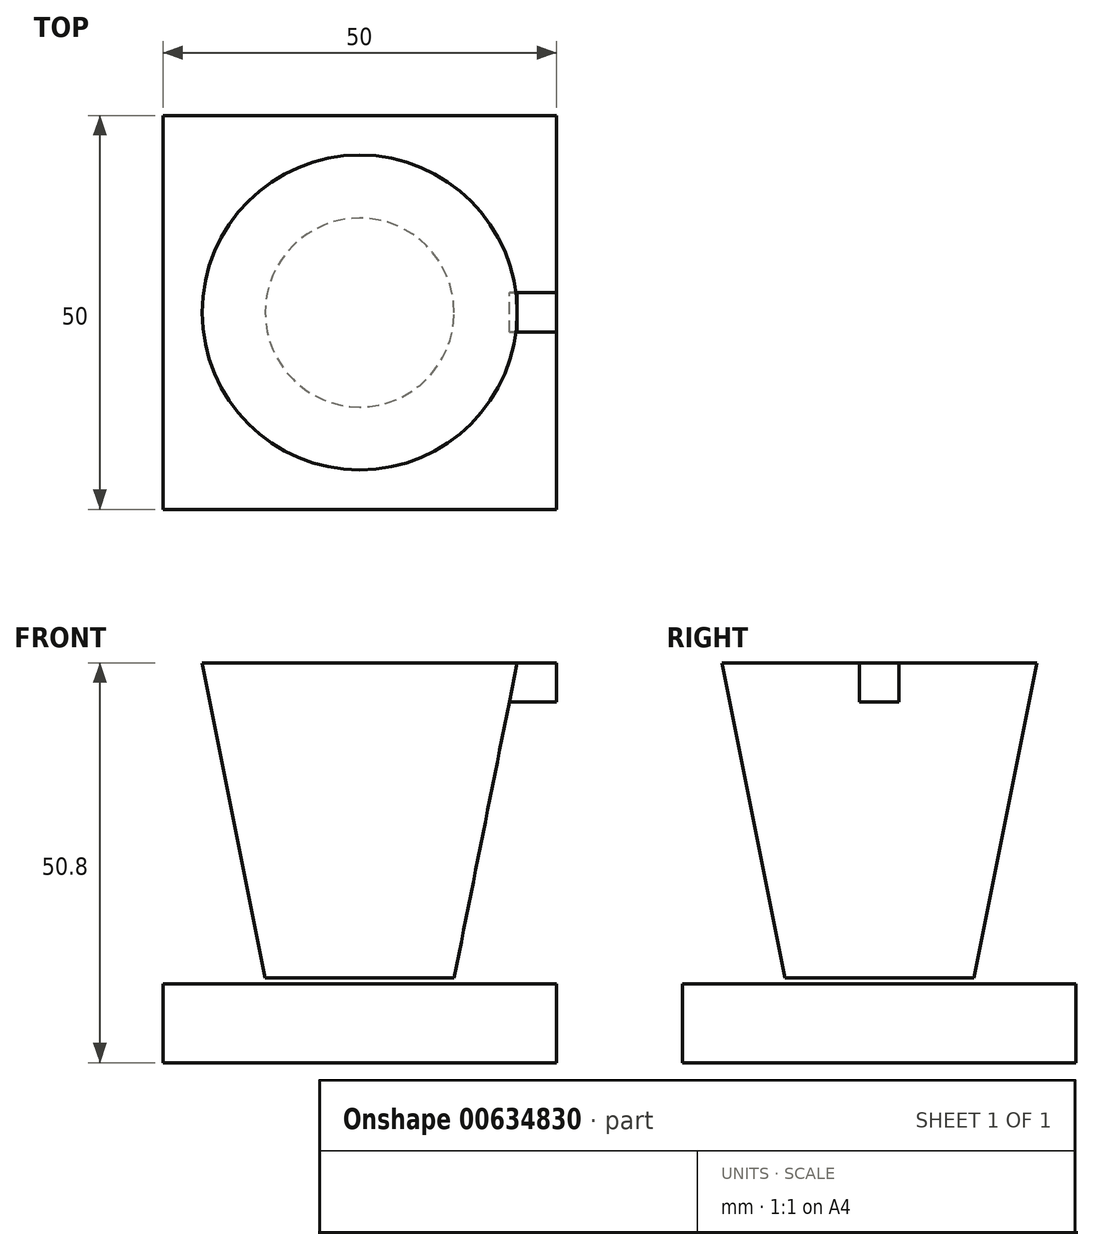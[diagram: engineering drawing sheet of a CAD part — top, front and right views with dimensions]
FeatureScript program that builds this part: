
annotation { "Feature Type Name" : "Feature", "Feature Type Description" : "" }
export const myFeature = defineFeature(function(context is Context, id is Id, definition is map)
    precondition{}
    {
        {
            var Q0;
            Q0=qCreatedBy(makeId("Front.planeOp"),FACE);
            var sketch = newSketch(context, id + "F0", { "sketchPlane" : qUnion([Q0])});
            skLineSegment(sketch, "E0.bottom", {"start": v(-25, 0) * mm, "end": v(25, 0) * mm});
            skLineSegment(sketch, "E0.top", {"start": v(-25, -10) * mm, "end": v(25, -10) * mm});
            skLineSegment(sketch, "E0.left", {"start": v(-25, 0) * mm, "end": v(-25, -10) * mm});
            skLineSegment(sketch, "E0.right", {"start": v(25, 0) * mm, "end": v(25, -10) * mm});
            skLineSegment(sketch, "E1", {"start": v(20, 40.8) * mm, "end": v(0, 40.8) * mm});
            skLineSegment(sketch, "E2", {"start": v(0, 40.8) * mm, "end": v(0, 0.8) * mm});
            skLineSegment(sketch, "E3.bottom", {"start": v(0, 40.8) * mm, "end": v(25, 40.8) * mm});
            skLineSegment(sketch, "E3.top", {"start": v(0, 35.8) * mm, "end": v(25, 35.8) * mm});
            skLineSegment(sketch, "E3.left", {"start": v(0, 40.8) * mm, "end": v(0, 35.8) * mm});
            skLineSegment(sketch, "E3.right", {"start": v(25, 40.8) * mm, "end": v(25, 35.8) * mm});
            skLineSegment(sketch, "E4.bottom", {"start": v(25, 35.8) * mm, "end": v(20, 35.8) * mm});
            skLineSegment(sketch, "E4.top", {"start": v(25, 0) * mm, "end": v(20, 0) * mm});
            skLineSegment(sketch, "E4.left", {"start": v(25, 35.8) * mm, "end": v(25, 0) * mm});
            skLineSegment(sketch, "E4.right", {"start": v(20, 35.8) * mm, "end": v(20, 0) * mm});
            skLineSegment(sketch, "E5", {"start": v(20, 40.8) * mm, "end": v(12, 0.8) * mm});
            skLineSegment(sketch, "E6", {"start": v(12, 0.8) * mm, "end": v(0, 0.8) * mm});
            skSolve(sketch);
        }
        {
            var Q0;
            Q0=makeQuery(id+"F0.imprint","IMPRINT",FACE,{"disambiguationData":[TD([[makeQuery(id+"F0.imprint","IMPRINT",EDGE,{"derivedFrom":sQuery(id+"F0.wireOp",EDGE,"E0.bottom")}),-1.0]])]});
            extrude(context, id + "F1", {"entities" : qUnion([Q0]), "endBound" : BoundingType.SYMMETRIC, "depth" : 50 * mm, "offsetDistance" : 25 * mm});
        }
        {
            var Q0;
            Q0=makeQuery(id+"F0.imprint","IMPRINT",FACE,{"disambiguationData":[TD([[makeQuery(id+"F0.imprint","IMPRINT",EDGE,{"derivedFrom":sQuery(id+"F0.wireOp",EDGE,"E4.bottom")}),1.0]])]});
            var Q1;
            {var subQ0=sQuery(id+"F0.wireOp",EDGE,"E3.right");Q1=makeQuery(id+"F0.imprint","IMPRINT",FACE,{"disambiguationData":[TD([[makeQuery(id+"F0.imprint","IMPRINT",EDGE,{"derivedFrom":subQ0}),-1.0]])]});}
            var Q2;
            {var subQ5=sQuery(id+"F0.wireOp",EDGE,"E3.left");Q2=makeQuery(id+"F0.imprint","IMPRINT",FACE,{"disambiguationData":[TD([[makeQuery(id+"F0.imprint","IMPRINT",EDGE,{"derivedFrom":subQ5}),1.0]])]});}
            extrude(context, id + "F2", {"entities" : qUnion([Q0, Q1, Q2]), "operationType" : NewBodyOperationType.ADD, "endBound" : BoundingType.SYMMETRIC, "depth" : 5 * mm, "offsetDistance" : 25 * mm});
        }
        {
            var Q0;
            {var subQ0=sQuery(id+"F0.wireOp",EDGE,"E2");Q0=makeQuery(id+"F0.imprint","IMPRINT",FACE,{"disambiguationData":[TD([[makeQuery(id+"F0.imprint","IMPRINT",EDGE,{"derivedFrom":subQ0}),1.0]])]});}
            var Q1;
            {var subQ5=sQuery(id+"F0.wireOp",EDGE,"E3.left");Q1=makeQuery(id+"F0.imprint","IMPRINT",FACE,{"disambiguationData":[TD([[makeQuery(id+"F0.imprint","IMPRINT",EDGE,{"derivedFrom":subQ5}),1.0]])]});}
            var Q2;
            Q2=sQuery(id+"F0.wireOp",EDGE,"E2");
            revolve(context, id + "F3", {"entities" : qUnion([Q0, Q1]), "axis" : qUnion([Q2]), "revolveType" : RevolveType.FULL});
        }
    });
